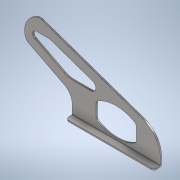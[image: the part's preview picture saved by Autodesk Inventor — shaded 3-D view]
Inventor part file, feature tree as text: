
AUTODESK INVENTOR PART (.ipt)
format: ipt  version: 2020 (Build 240168000, 168)  size: 268,800 bytes
history: native  units: mm
features: other x3, extrude x2, sketch x1, projected_geometry x1
ambient origin geometry x8: Origin, YZ Plane, XZ Plane, XY Plane, X Axis, Y Axis, Z Axis, Center Point
bodies: Body1 (feature_tree)
feature tree (7):
  other  "實體1"
  extrude  "擠出1"  Depth=120.0mm
  other  "折彎零件1"
  extrude  "手工切除2.5"  Depth=3.5mm
  sketch  "草圖2"
  projected_geometry  "投影迴路1"
  other  "定義1"
